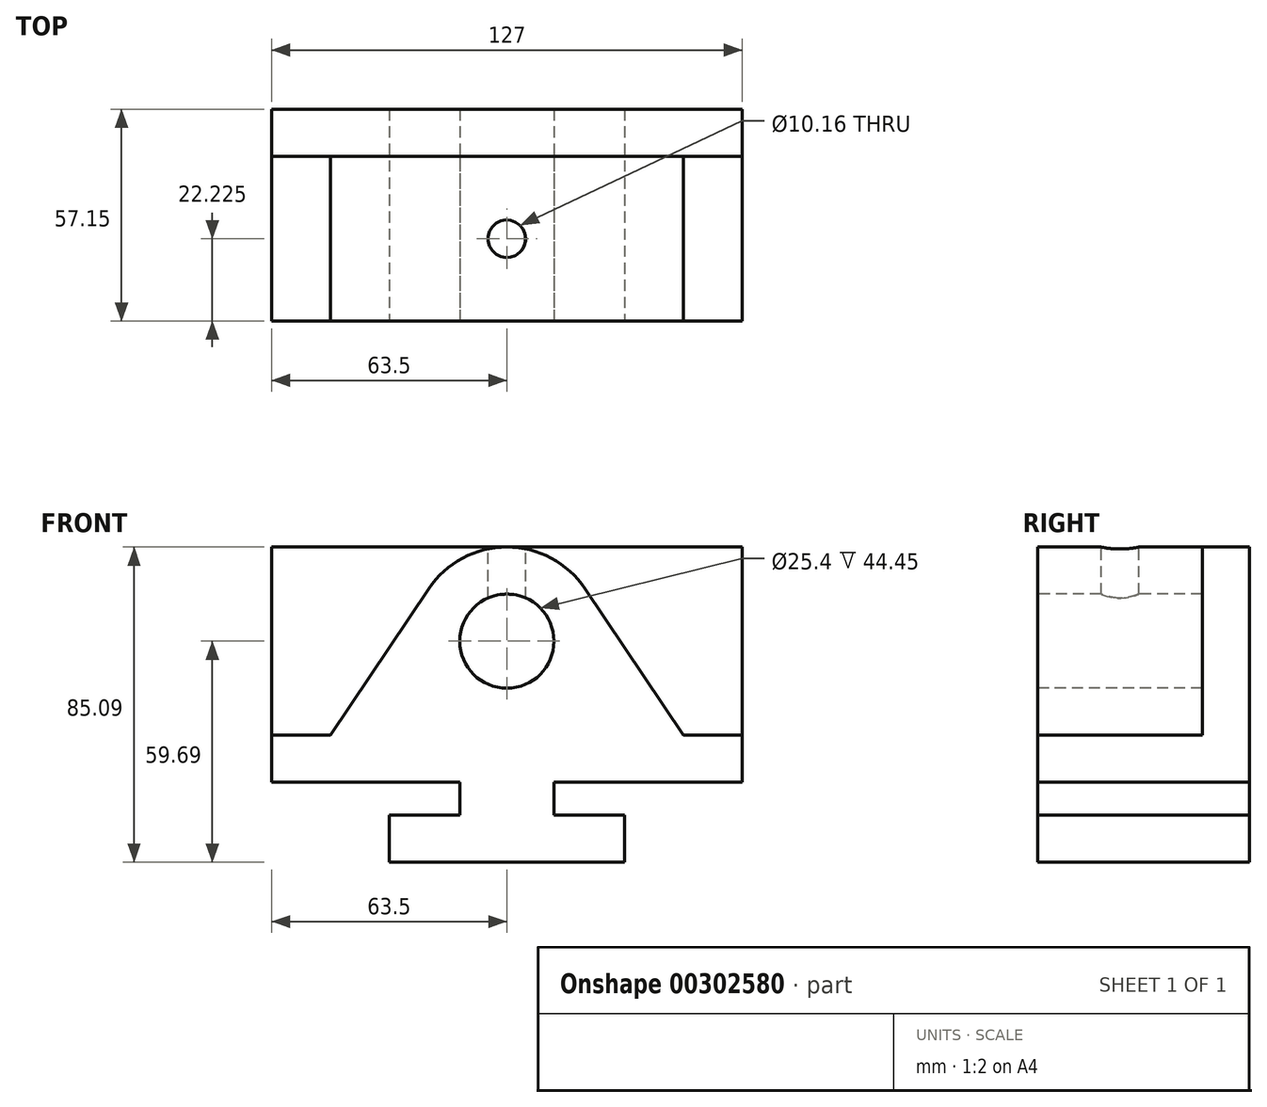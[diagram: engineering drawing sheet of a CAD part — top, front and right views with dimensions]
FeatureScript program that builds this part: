
annotation { "Feature Type Name" : "Feature", "Feature Type Description" : "" }
export const myFeature = defineFeature(function(context is Context, id is Id, definition is map)
    precondition{}
    {
        {
            var Q0;
            Q0=qCreatedBy(makeId("Front.planeOp"),FACE);
            var sketch = newSketch(context, id + "F0", { "sketchPlane" : qUnion([Q0])});
            skLineSegment(sketch, "E0.bottom", {"start": v(0, 0) * mm, "end": v(127, 0) * mm});
            skLineSegment(sketch, "E0.top", {"start": v(0, 85.1) * mm, "end": v(127, 85.1) * mm});
            skLineSegment(sketch, "E0.left", {"start": v(0, 0) * mm, "end": v(0, 85.1) * mm});
            skLineSegment(sketch, "E0.right", {"start": v(127, 0) * mm, "end": v(127, 85.1) * mm});
            skSolve(sketch);
        }
        {
            var Q0;
            Q0 = qSketchRegion(id + "F0", true);
            extrude(context, id + "F1", {"entities" : qUnion([Q0]), "depth" : 57.15 * mm});
        }
        {
            var Q0;
            Q0=makeQuery(id+"F1.opExtrude","CAP_FACE",FACE,{"disambiguationData":[OSD([sQuery(id+"F0.wireOp",EDGE,"E0.bottom"),sQuery(id+"F0.wireOp",EDGE,"E0.top"),sQuery(id+"F0.wireOp",EDGE,"E0.left"),sQuery(id+"F0.wireOp",EDGE,"E0.right")])],"isStart":false});
            var sketch = newSketch(context, id + "F2", { "sketchPlane" : qUnion([Q0])});
            skLineSegment(sketch, "E1", {"start": v(63.5, 85.1) * mm, "end": v(63.5, 0) * mm, "construction": true});
            skLineSegment(sketch, "E2.0", {"start": v(31.75, 0) * mm, "end": v(63.5, 0) * mm});
            skLineSegment(sketch, "E3", {"start": v(31.75, 0) * mm, "end": v(31.75, 12.7) * mm});
            skLineSegment(sketch, "E4", {"start": v(31.75, 12.7) * mm, "end": v(50.8, 12.7) * mm});
            skLineSegment(sketch, "E5", {"start": v(50.8, 12.7) * mm, "end": v(50.8, 21.6) * mm});
            skLineSegment(sketch, "E6", {"start": v(50.8, 21.6) * mm, "end": v(0, 21.59) * mm});
            skPoint(sketch, "E7.orphan", {"position": v(0, 0) * mm});
            skPoint(sketch, "E8.orphan", {"position": v(127, 0) * mm});
            skLineSegment(sketch, "E9.MirrorCS", {"start": v(76.2, 12.7) * mm, "end": v(76.2, 21.6) * mm});
            skLineSegment(sketch, "E10.MirrorCS", {"start": v(76.2, 21.6) * mm, "end": v(127, 21.59) * mm});
            skLineSegment(sketch, "E11.MirrorCS", {"start": v(95.25, 12.7) * mm, "end": v(76.2, 12.7) * mm});
            skLineSegment(sketch, "E12.MirrorCS", {"start": v(95.25, 0) * mm, "end": v(63.5, 0) * mm});
            skLineSegment(sketch, "E13.MirrorCS", {"start": v(95.25, 0) * mm, "end": v(95.25, 12.7) * mm});
            skSolve(sketch);
        }
        {
            var Q0;
            {var subQ4=sQuery(id+"F2.wireOp",EDGE,"E3");Q0=makeQuery(id+"F2.imprint","IMPRINT",FACE,{"disambiguationData":[TD([[makeQuery(id+"F2.imprint","IMPRINT",EDGE,{"derivedFrom":subQ4}),1.0]])]});}
            var Q1;
            Q1=makeQuery(id+"F2.imprint","IMPRINT",FACE,{"disambiguationData":[TD([[makeQuery(id+"F2.imprint","IMPRINT",EDGE,{"derivedFrom":sQuery(id+"F2.wireOp",EDGE,"E9.MirrorCS")}),-1.0]])]});
            extrude(context, id + "F3", {"entities" : qUnion([Q0, Q1]), "operationType" : NewBodyOperationType.REMOVE, "endBound" : BoundingType.THROUGH_ALL, "oppositeDirection" : true, "depth" : 25.4 * mm});
        }
        {
            var Q0;
            Q0=makeQuery(id+"F1.opExtrude","CAP_FACE",FACE,{"disambiguationData":[OSD([sQuery(id+"F0.wireOp",EDGE,"E0.bottom"),sQuery(id+"F0.wireOp",EDGE,"E0.top"),sQuery(id+"F0.wireOp",EDGE,"E0.left"),sQuery(id+"F0.wireOp",EDGE,"E0.right")])],"isStart":false});
            var sketch = newSketch(context, id + "F4", { "sketchPlane" : qUnion([Q0])});
            skLineSegment(sketch, "E14.0", {"start": v(0, 21.59) * mm, "end": v(0, 34.3) * mm});
            skLineSegment(sketch, "E15", {"start": v(0, 34.3) * mm, "end": v(15.88, 34.3) * mm});
            skLineSegment(sketch, "E16", {"start": v(63.5, 85.1) * mm, "end": v(63.5, 0) * mm, "construction": true});
            skLineSegment(sketch, "E17", {"start": v(15.88, 34.3) * mm, "end": v(42.4, 73.84) * mm});
            skArc(sketch, "E18.filletArc", {"start": v(84.6, 73.84) * mm, "mid": v(63.5, 85.1) * mm, "end": v(42.4, 73.84) * mm});
            skLineSegment(sketch, "E19.MirrorCS", {"start": v(111.13, 34.3) * mm, "end": v(84.6, 73.84) * mm});
            skLineSegment(sketch, "E20.MirrorCS", {"start": v(127, 21.59) * mm, "end": v(127, 34.3) * mm});
            skLineSegment(sketch, "E21.MirrorCS", {"start": v(127, 34.3) * mm, "end": v(111.12, 34.3) * mm});
            skCircle(sketch, "E22", {"center": v(63.5, 59.7) * mm, "radius": 12.7 * mm});
            skSolve(sketch);
        }
        {
            var Q0;
            Q0=makeQuery(id+"F4.imprint","IMPRINT",FACE,{"disambiguationData":[TD([[makeQuery(id+"F4.imprint","IMPRINT",EDGE,{"derivedFrom":sQuery(id+"F4.wireOp",EDGE,"E22")}),1.0]])]});
            var Q1;
            {var subQ3=sQuery(id+"F4.wireOp",EDGE,"E15");Q1=makeQuery(id+"F4.imprint","IMPRINT",FACE,{"disambiguationData":[TD([[makeQuery(id+"F4.imprint","IMPRINT",EDGE,{"derivedFrom":subQ3}),1.0]])]});}
            var Q2;
            {var subQ4=sQuery(id+"F4.wireOp",EDGE,"E19.MirrorCS");Q2=makeQuery(id+"F4.imprint","IMPRINT",FACE,{"disambiguationData":[TD([[makeQuery(id+"F4.imprint","IMPRINT",EDGE,{"derivedFrom":subQ4}),-1.0]])]});}
            extrude(context, id + "F5", {"entities" : qUnion([Q0, Q1, Q2]), "operationType" : NewBodyOperationType.REMOVE, "oppositeDirection" : true, "depth" : 44.45 * mm});
        }
        {
            var Q0;
            Q0=makeQuery(id+"F1.opExtrude","SWEPT_FACE",FACE,{"disambiguationData":[OSD([sQuery(id+"F0.wireOp",EDGE,"E0.top")])]});
            var sketch = newSketch(context, id + "F6", { "sketchPlane" : qUnion([Q0])});
            skLineSegment(sketch, "E23", {"start": v(63.5, 0) * mm, "end": v(63.5, -57.57) * mm, "construction": true});
            skCircle(sketch, "E24", {"center": v(63.5, -34.93) * mm, "radius": 5.08 * mm});
            skSolve(sketch);
        }
        {
            var Q0;
            Q0 = qSketchRegion(id + "F6", true);
            var Q1;
            Q1=makeQuery(id+"F5.boolean.opBoolean","COPY",FACE,{"derivedFrom":makeQuery(id+"F5.opExtrude","SWEPT_FACE",FACE,{"disambiguationData":[OSD([sQuery(id+"F4.wireOp",EDGE,"E22")])]})});
            extrude(context, id + "F7", {"entities" : qUnion([Q0]), "operationType" : NewBodyOperationType.REMOVE, "endBound" : BoundingType.UP_TO_SURFACE, "oppositeDirection" : true, "endBoundEntityFace" : qUnion([Q1]), "depth" : 25.4 * mm});
        }
    });
